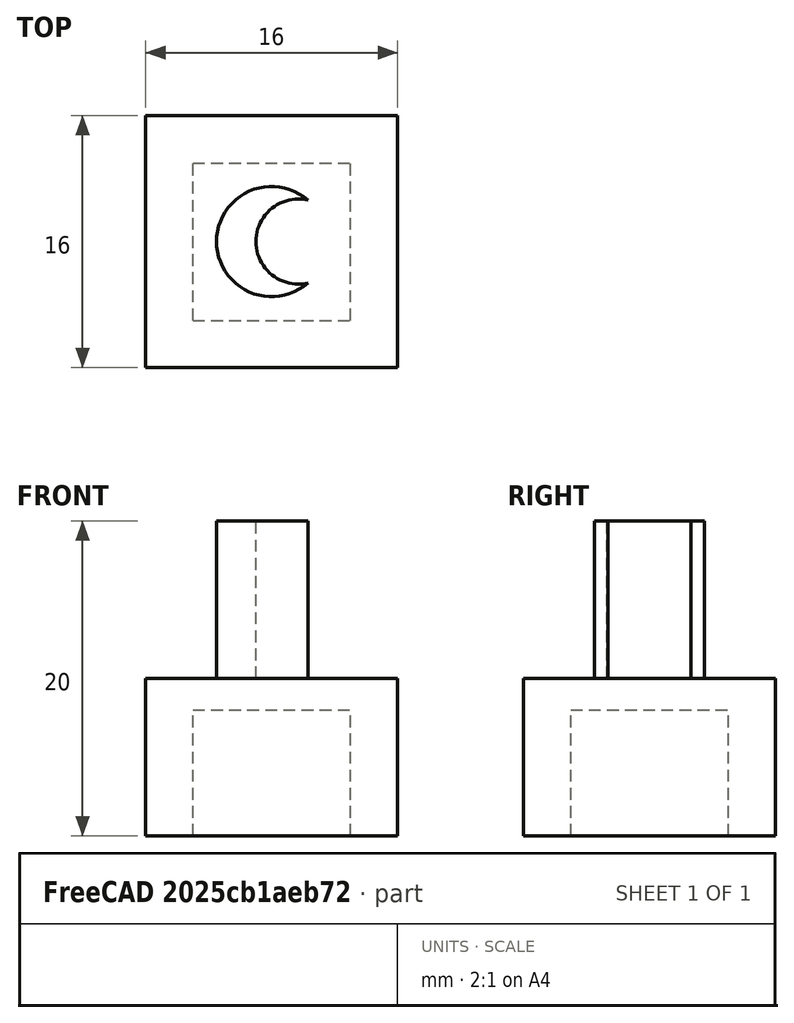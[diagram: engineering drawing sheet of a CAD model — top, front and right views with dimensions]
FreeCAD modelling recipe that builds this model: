
FCSTD DOCUMENT  (FreeCAD 0.18.3R)
Label: moon
License: All rights reserved
LicenseURL: http://en.wikipedia.org/wiki/All_rights_reserved
objects: Part::Box×2, Part::Cylinder×2, Part::Cut×2, Part::Fuse×1
note: 7 computed .brp shape members not serialized (recipe doc carries the construction recipe); baked Part::Feature solids carry a one-line shape summary decoded from their .brp

FEATURE [Part::Box] Box  label="Cube"
  AttacherType = Attacher::AttachEngine3D
  Height = 10
  Length = 16
  Placement = pos=(-8,-8,0) rot=(0,0,1;0rad)
  Width = 16
FEATURE [Part::Cylinder] Cylinder
  Angle = 360
  AttacherType = Attacher::AttachEngine3D
  Height = 10
  Placement = pos=(1.7,0,10) rot=(0,0,1;0rad)
  Radius = 2.7
FEATURE [Part::Cylinder] Cylinder001
  Angle = 360
  AttacherType = Attacher::AttachEngine3D
  Height = 10
  Placement = pos=(0,0,10) rot=(0,0,1;0rad)
  Radius = 3.5
FEATURE [Part::Cut] Cut
  Base = -> Cylinder001
  Tool = -> Cylinder
FEATURE [Part::Fuse] Fusion
  Base = -> Box
  Tool = -> Cut
FEATURE [Part::Box] Box001  label="Cube001"
  AttacherType = Attacher::AttachEngine3D
  Height = 8
  Length = 10
  Placement = pos=(-5,-5,0) rot=(0,0,1;0rad)
  Width = 10
FEATURE [Part::Cut] Cut001
  Base = -> Fusion
  Tool = -> Box001
